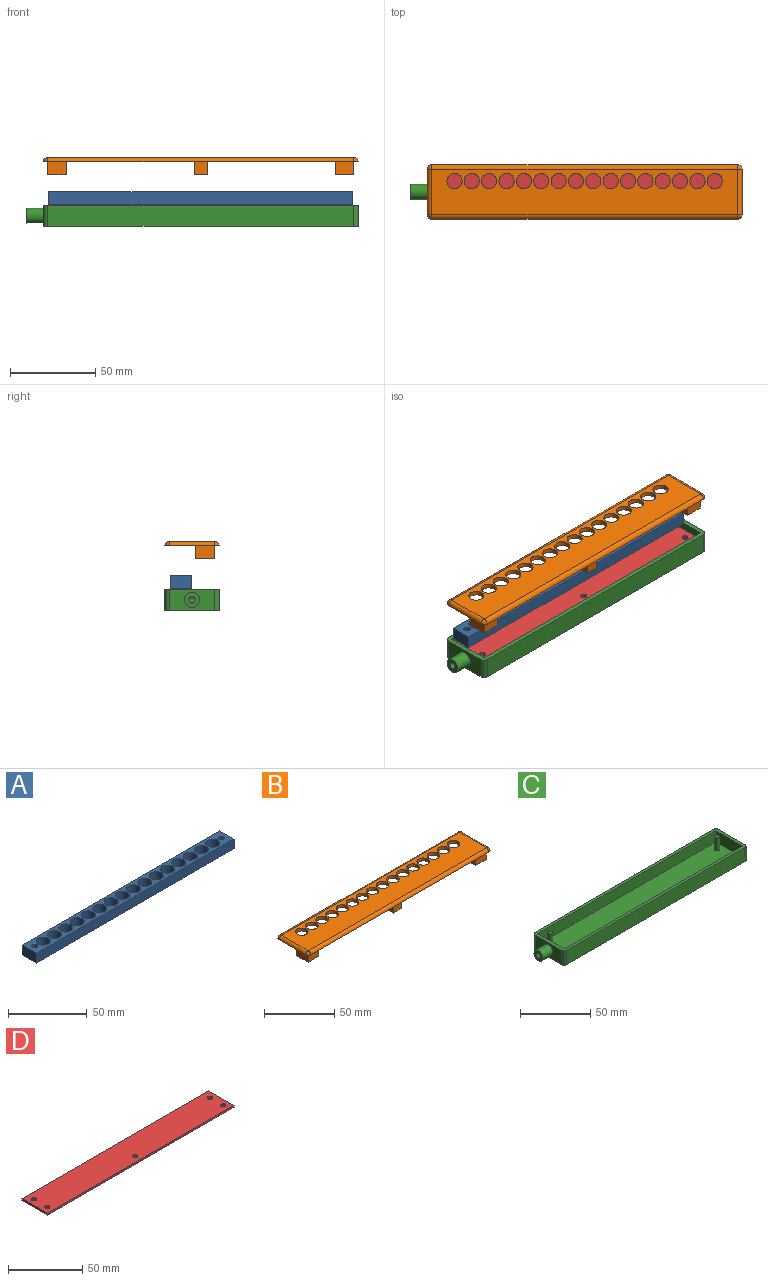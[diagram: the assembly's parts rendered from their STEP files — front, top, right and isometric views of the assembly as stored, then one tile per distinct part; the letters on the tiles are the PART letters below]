
ASSEMBLY  parts=4 mates=3
PART A: 24 faces, bbox 177.8x12.7x7.6 mm
  f0: plane 177.8x7.62mm, normal (0,1,0), area 1354.8mm2, adj f1,f21,f22,f23
  f1: plane 12.7x7.62mm, normal (-1,0,0), area 96.8mm2, adj f0,f2,f22,f23
  f2: plane 177.8x7.62mm, normal (0,-1,0), area 1354.8mm2, adj f1,f21,f22,f23
  f3: cylinder r=1.91mm len=7.62mm, axis (0,0,-1), area 91.2mm2, adj f22,f23
  f4: cylinder r=1.91mm len=7.62mm, axis (0,0,-1), area 91.2mm2, adj f22,f23
  f5: cylinder r=4.45mm len=8.89mm, axis (0,0,-1), area 212.8mm2, adj f22,f23
  f6: cylinder r=4.45mm len=8.89mm, axis (0,0,-1), area 212.8mm2, adj f22,f23
  f7: cylinder r=4.45mm len=8.89mm, axis (0,0,-1), area 212.8mm2, adj f22,f23
  f8: cylinder r=4.45mm len=8.89mm, axis (0,0,-1), area 212.8mm2, adj f22,f23
  f9: cylinder r=4.45mm len=8.89mm, axis (0,0,-1), area 212.8mm2, adj f22,f23
  f10: cylinder r=4.45mm len=8.89mm, axis (0,0,-1), area 212.8mm2, adj f22,f23
  f11: cylinder r=4.45mm len=8.89mm, axis (0,0,-1), area 212.8mm2, adj f22,f23
  f12: cylinder r=4.45mm len=8.89mm, axis (0,0,-1), area 212.8mm2, adj f22,f23
  f13: cylinder r=4.45mm len=8.89mm, axis (0,0,-1), area 212.8mm2, adj f22,f23
  f14: cylinder r=4.45mm len=8.89mm, axis (0,0,-1), area 212.8mm2, adj f22,f23
  f15: cylinder r=4.45mm len=8.89mm, axis (0,0,-1), area 212.8mm2, adj f22,f23
  f16: cylinder r=4.45mm len=8.89mm, axis (0,0,-1), area 212.8mm2, adj f22,f23
  f17: cylinder r=4.45mm len=8.89mm, axis (0,0,-1), area 212.8mm2, adj f22,f23
  f18: cylinder r=4.45mm len=8.89mm, axis (0,0,-1), area 212.8mm2, adj f22,f23
  f19: cylinder r=4.45mm len=8.89mm, axis (0,0,-1), area 212.8mm2, adj f22,f23
  f20: cylinder r=4.45mm len=8.89mm, axis (0,0,-1), area 212.8mm2, adj f22,f23
  f21: plane 12.7x7.62mm, normal (1,0,0), area 96.8mm2, adj f0,f2,f22,f23
  f22: plane 177.8x12.7mm, normal (0,0,1), area 1242.1mm2, adj f0,f1,f2,f3,f4,f5,f6,f7
  f23: plane 177.8x12.7mm, normal (0,0,-1), area 1242.1mm2, adj f0,f1,f2,f3,f4,f5,f6,f7
PART B: 55 faces, bbox 184.2x31.8x10.2 mm
  f0: plane 179.07x26.67mm, normal (0,0,1), area 3782.7mm2, adj f3,f4,f7,f8,f39,f40,f41,f42
  f1: plane 184.15x31.75mm, normal (0,0,-1), area 4512.4mm2, adj f2,f3,f4,f5,f6,f7,f8,f9
  f2: sphere r=2.54mm, area 10.1mm2, adj f1,f3,f4
  f3: cylinder r=2.54mm len=26.67mm, axis (0,-1,0), area 106.4mm2, adj f0,f1,f2,f5
  f4: cylinder r=2.54mm len=179.07mm, axis (-1,0,0), area 714.5mm2, adj f0,f1,f2,f6
  f5: sphere r=2.54mm, area 10.1mm2, adj f1,f3,f7
  f6: sphere r=2.54mm, area 10.1mm2, adj f1,f4,f8
  f7: cylinder r=2.54mm len=179.07mm, axis (1,0,0), area 714.5mm2, adj f0,f1,f5,f9
  f8: cylinder r=2.54mm len=26.67mm, axis (0,1,0), area 106.4mm2, adj f0,f1,f6,f9
  f9: sphere r=2.54mm, area 10.1mm2, adj f1,f7,f8
  f10: plane 10.74x7.62mm, normal (1,0,0), area 81.9mm2, adj f1,f11,f13,f14
  f11: plane 10.74x7.62mm, normal (0,-1,0), area 81.9mm2, adj f1,f10,f12,f14
  f12: plane 7.62x7.16mm, normal (-1,0,0), area 54.6mm2, adj f1,f11,f14,f38
  f13: plane 7.62x7.16mm, normal (0,1,0), area 54.6mm2, adj f1,f10,f14,f38
  f14: plane 10.74x10.74mm, normal (0,0,-1), area 104.8mm2, adj f10,f11,f12,f13,f33,f38
  f15: plane 7.62x7.62mm, normal (0,-1,0), area 58.1mm2, adj f1,f16,f18,f19
  f16: plane 7.85x7.62mm, normal (-1,0,0), area 59.8mm2, adj f1,f15,f19,f36
  f17: plane 7.62x0.46mm, normal (0,1,0), area 3.5mm2, adj f1,f19,f36,f37
  f18: plane 7.85x7.62mm, normal (1,0,0), area 59.8mm2, adj f1,f15,f19,f37
  f19: plane 11.43x7.62mm, normal (0,0,-1), area 73.7mm2, adj f15,f16,f17,f18,f31,f36,f37
  f20: plane 10.74x7.62mm, normal (0,-1,0), area 81.9mm2, adj f1,f21,f23,f24
  f21: plane 11.43x7.62mm, normal (-1,0,0), area 87.1mm2, adj f1,f20,f22,f24
  f22: plane 7.62x7.16mm, normal (0,1,0), area 54.6mm2, adj f1,f21,f24,f35
  f23: plane 7.85x7.62mm, normal (1,0,0), area 59.8mm2, adj f1,f20,f24,f35
  f24: plane 11.43x10.74mm, normal (0,0,-1), area 112.1mm2, adj f20,f21,f22,f23,f29,f35
  f25: cylinder r=1.84mm len=3.68mm, axis (0,0,-1), area 17.6mm2, adj f1,f26
  f26: plane 3.68x3.68mm, normal (0,0,-1), area 10.7mm2, adj f25
  f27: cylinder r=1.84mm len=3.68mm, axis (0,0,-1), area 17.6mm2, adj f1,f28
  f28: plane 3.68x3.68mm, normal (0,0,-1), area 10.7mm2, adj f27
  f29: cylinder r=1.59mm len=7.62mm, axis (0,0,1), area 76mm2, adj f24,f30
  f30: plane 3.18x3.18mm, normal (0,0,-1), area 7.9mm2, adj f29
  f31: cylinder r=1.59mm len=7.62mm, axis (0,0,1), area 76mm2, adj f19,f32
  f32: plane 3.18x3.18mm, normal (0,0,-1), area 7.9mm2, adj f31
  f33: cylinder r=1.59mm len=7.62mm, axis (0,0,1), area 76mm2, adj f14,f34
  f34: plane 3.18x3.18mm, normal (0,0,-1), area 7.9mm2, adj f33
  f35: cylinder r=3.58mm len=7.62mm, axis (0,0,-1), area 42.9mm2, adj f1,f22,f23,f24
  f36: cylinder r=3.58mm len=7.62mm, axis (0,0,1), area 42.9mm2, adj f1,f16,f17,f19
  f37: cylinder r=3.58mm len=7.62mm, axis (0,0,-1), area 42.9mm2, adj f1,f17,f18,f19
  f38: cylinder r=3.58mm len=7.62mm, axis (0,0,-1), area 42.9mm2, adj f1,f12,f13,f14
  f39: cylinder r=4.45mm len=8.89mm, axis (0,0,1), area 70.9mm2, adj f0,f1
  f40: cylinder r=4.45mm len=8.89mm, axis (0,0,1), area 70.9mm2, adj f0,f1
  f41: cylinder r=4.45mm len=8.89mm, axis (0,0,1), area 70.9mm2, adj f0,f1
  f42: cylinder r=4.45mm len=8.89mm, axis (0,0,1), area 70.9mm2, adj f0,f1
  f43: cylinder r=4.45mm len=8.89mm, axis (0,0,1), area 70.9mm2, adj f0,f1
  f44: cylinder r=4.45mm len=8.89mm, axis (0,0,1), area 70.9mm2, adj f0,f1
  f45: cylinder r=4.45mm len=8.89mm, axis (0,0,1), area 70.9mm2, adj f0,f1
  f46: cylinder r=4.45mm len=8.89mm, axis (0,0,1), area 70.9mm2, adj f0,f1
  f47: cylinder r=4.45mm len=8.89mm, axis (0,0,1), area 70.9mm2, adj f0,f1
  f48: cylinder r=4.45mm len=8.89mm, axis (0,0,1), area 70.9mm2, adj f0,f1
  f49: cylinder r=4.45mm len=8.89mm, axis (0,0,1), area 70.9mm2, adj f0,f1
  f50: cylinder r=4.45mm len=8.89mm, axis (0,0,1), area 70.9mm2, adj f0,f1
  f51: cylinder r=4.45mm len=8.89mm, axis (0,0,1), area 70.9mm2, adj f0,f1
  f52: cylinder r=4.45mm len=8.89mm, axis (0,0,1), area 70.9mm2, adj f0,f1
  f53: cylinder r=4.45mm len=8.89mm, axis (0,0,1), area 70.9mm2, adj f0,f1
  f54: cylinder r=4.45mm len=8.89mm, axis (0,0,1), area 70.9mm2, adj f0,f1
PART C: 25 faces, bbox 194.3x31.8x13.9 mm
  f0: plane 184.15x31.75mm, normal (0,0,1), area 1065.4mm2, adj f1,f2,f3,f4,f6,f7,f8,f9
  f1: plane 26.67x12.38mm, normal (-1,0,0), area 268.2mm2, adj f0,f5,f15,f18,f22
  f2: plane 179.07x12.38mm, normal (0,-1,0), area 2217.3mm2, adj f0,f5,f15,f16
  f3: plane 26.67x12.38mm, normal (1,0,0), area 330.2mm2, adj f0,f5,f16,f17
  f4: plane 179.07x12.38mm, normal (0,1,0), area 2217.3mm2, adj f0,f5,f17,f18
  f5: plane 184.15x31.75mm, normal (0,0,-1), area 5811.2mm2, adj f1,f2,f3,f4,f15,f16,f17,f18
  f6: plane 179.07x9.84mm, normal (0,1,0), area 1762.5mm2, adj f0,f7,f9,f10
  f7: plane 26.67x9.84mm, normal (-1,0,0), area 262.5mm2, adj f0,f6,f8,f10
  f8: plane 179.07x9.84mm, normal (0,-1,0), area 1762.5mm2, adj f0,f7,f9,f10
  f9: plane 26.67x9.84mm, normal (1,0,0), area 251.1mm2, adj f0,f6,f8,f10,f24
  f10: plane 179.07x26.67mm, normal (0,0,1), area 4725.7mm2, adj f6,f7,f8,f9,f11,f13,f19,f20
  f11: cylinder r=1.79mm len=11.33mm, axis (0,0,-1), area 127.1mm2, adj f10,f12
  f12: plane 3.57x3.57mm, normal (0,0,1), area 10mm2, adj f11
  f13: cylinder r=1.79mm len=11.33mm, axis (0,0,-1), area 127.1mm2, adj f10,f14
  f14: plane 3.57x3.57mm, normal (0,0,1), area 10mm2, adj f13
  f15: cylinder r=2.54mm len=12.38mm, axis (0,0,1), area 49.4mm2, adj f0,f1,f2,f5
  f16: cylinder r=2.54mm len=12.38mm, axis (0,0,-1), area 49.4mm2, adj f0,f2,f3,f5
  f17: cylinder r=2.54mm len=12.38mm, axis (0,0,1), area 49.4mm2, adj f0,f3,f4,f5
  f18: cylinder r=2.54mm len=12.38mm, axis (0,0,-1), area 49.4mm2, adj f0,f1,f4,f5
  f19: cylinder r=1.79mm len=3.57mm, axis (0,0,1), area 28.5mm2, adj f5,f10
  f20: cylinder r=1.79mm len=3.57mm, axis (0,0,1), area 28.5mm2, adj f5,f10
  f21: cylinder r=1.79mm len=3.57mm, axis (0,0,1), area 28.5mm2, adj f5,f10
  f22: cylinder r=4.45mm len=10.16mm, axis (1,0,0), area 283.8mm2, adj f1,f23
  f23: plane 8.89x8.89mm, normal (-1,0,0), area 50.7mm2, adj f22,f24
  f24: cylinder r=1.91mm len=12.7mm, axis (-1,0,0), area 152mm2, adj f9,f23
PART D: 11 faces, bbox 177.8x24.1x1.6 mm
  f0: plane 177.8x1.59mm, normal (0,1,0), area 282.3mm2, adj f1,f8,f9,f10
  f1: plane 24.13x1.59mm, normal (-1,0,0), area 38.3mm2, adj f0,f2,f9,f10
  f2: plane 177.8x1.59mm, normal (0,-1,0), area 282.3mm2, adj f1,f8,f9,f10
  f3: cylinder r=1.79mm len=3.57mm, axis (0,0,-1), area 17.8mm2, adj f9,f10
  f4: cylinder r=1.79mm len=3.57mm, axis (0,0,-1), area 17.8mm2, adj f9,f10
  f5: cylinder r=1.79mm len=3.57mm, axis (0,0,-1), area 17.8mm2, adj f9,f10
  f6: cylinder r=1.79mm len=3.57mm, axis (0,0,-1), area 17.8mm2, adj f9,f10
  f7: cylinder r=1.79mm len=3.57mm, axis (0,0,-1), area 17.8mm2, adj f9,f10
  f8: plane 24.13x1.59mm, normal (1,0,0), area 38.3mm2, adj f0,f2,f9,f10
  f9: plane 177.8x24.13mm, normal (0,0,1), area 4240.2mm2, adj f0,f1,f2,f3,f4,f5,f6,f7
  f10: plane 177.8x24.13mm, normal (0,0,-1), area 4240.2mm2, adj f0,f1,f2,f3,f4,f5,f6,f7
PLACE A t=(-23.7,20.54,-4.67)mm
PLACE B t=(-26.88,104.21,20.47)mm
PLACE C t=(-26.88,40.44,-17.27)mm fixed
PLACE D t=(-23.7,72.57,-10.45)mm
MATE slider C.f11 <-> D.f4  axis (0,0,-1) through (-18.62,62.67,-14.73)mm
MATE slider D.f4 <-> A.f3  axis (0,0,1) through (-18.62,62.67,-8.87)mm
MATE slider D.f3 <-> B.f29  axis (0,0,1) through (-18.62,49.97,-8.87)mm
